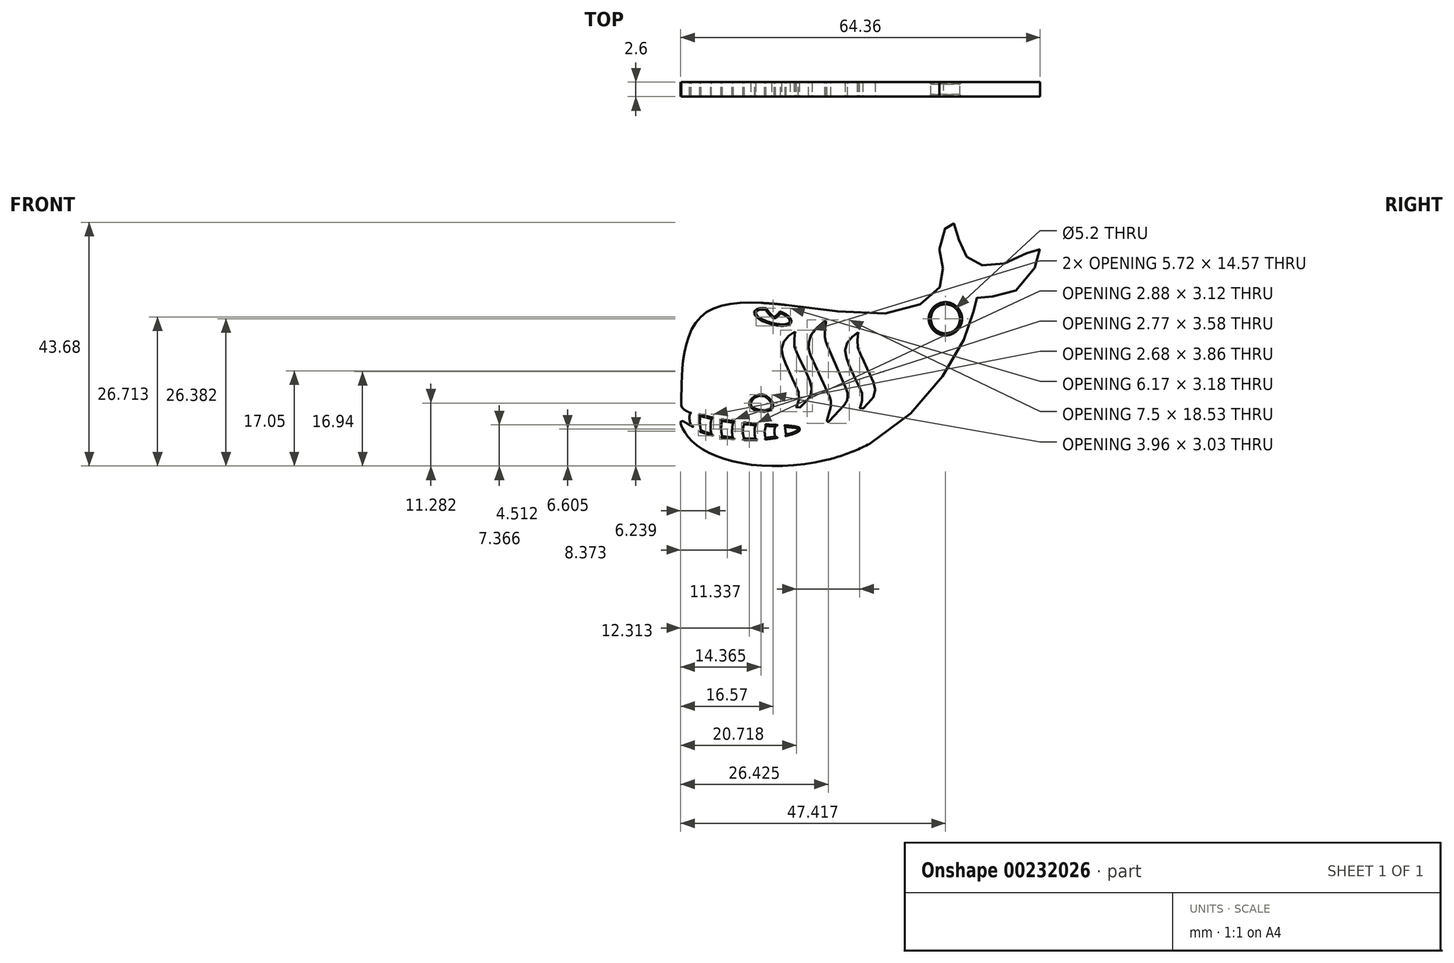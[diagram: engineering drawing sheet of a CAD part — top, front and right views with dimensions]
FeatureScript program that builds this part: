
annotation { "Feature Type Name" : "Feature", "Feature Type Description" : "" }
export const myFeature = defineFeature(function(context is Context, id is Id, definition is map)
    precondition{}
    {
        {
            var Q0;
            Q0=qCreatedBy(makeId("Front.planeOp"),FACE);
            var sketch = newSketch(context, id + "F0", { "sketchPlane" : qUnion([Q0])});
            skFitSpline(sketch, "E0", {"points": [v(-22.86, -10.44) * mm, v(-19.7, 1.07) * mm, v(5.67, 1.15) * mm, v(13.2, 5.95) * mm, v(12.7, 10.48) * mm, v(14.38, 13.69) * mm, v(15.38, 11.35) * mm, v(17.48, 8.08) * mm, v(23.08, 8.54) * mm, v(26.5, 9.96) * mm, v(23.05, 4.16) * mm, v(18, 3.34) * mm, v(17.28, 0.82) * mm, v(3.33, -16.7) * mm, v(-20.33, -17.35) * mm, v(-22.9, -13.75) * mm, v(-20.76, -14.75) * mm, v(-11.12, -16.02) * mm, v(-6.74, -14.84) * mm, v(-13.25, -14.23) * mm, v(-22.52, -12.08) * mm, v(-22.86, -10.44) * mm]});
            skFitSpline(sketch, "E1", {"points": [v(-5.34, -13.25) * mm, v(-5.6, -16.16) * mm, v(-1.36, -19.66) * mm, v(4.85, -18.8) * mm, v(4.28, -17.36) * mm, v(0.7, -15.99) * mm, v(-0.53, -13.57) * mm], "startDerivative": vector(-7.24, -19.66) * mm, "endDerivative": vector(-6.35, 20.95) * mm});
            skArc(sketch, "E2", {"start": v(-22.52, -12.08) * mm, "mid": v(-22.6, -12.94) * mm, "end": v(-22.52, -13.8) * mm});
            skArc(sketch, "E3", {"start": v(-21.63, -12.56) * mm, "mid": v(-21.72, -13.48) * mm, "end": v(-21.48, -14.38) * mm});
            skArc(sketch, "E4", {"start": v(-20.25, -13.02) * mm, "mid": v(-20.3, -14.02) * mm, "end": v(-20.15, -15) * mm});
            skArc(sketch, "E5", {"start": v(-18.7, -13.4) * mm, "mid": v(-18.83, -14.43) * mm, "end": v(-18.73, -15.45) * mm});
            skArc(sketch, "E6", {"start": v(-17.26, -13.69) * mm, "mid": v(-17.37, -14.74) * mm, "end": v(-17.22, -15.78) * mm});
            skArc(sketch, "E7", {"start": v(-15.7, -13.94) * mm, "mid": v(-15.86, -14.96) * mm, "end": v(-15.79, -15.98) * mm});
            skArc(sketch, "E8", {"start": v(-14.18, -14.13) * mm, "mid": v(-14.39, -15.11) * mm, "end": v(-14.2, -16.1) * mm});
            skArc(sketch, "E9", {"start": v(-12.64, -14.28) * mm, "mid": v(-12.77, -15.2) * mm, "end": v(-12.66, -16.11) * mm});
            skArc(sketch, "E10", {"start": v(-11.18, -14.38) * mm, "mid": v(-11.37, -15.2) * mm, "end": v(-11.23, -16.03) * mm});
            skArc(sketch, "E11", {"start": v(-9.9, -14.44) * mm, "mid": v(-10.05, -15.15) * mm, "end": v(-9.9, -15.86) * mm});
            skArc(sketch, "E12", {"start": v(-8.53, -14.52) * mm, "mid": v(-8.52, -15.04) * mm, "end": v(-8.4, -15.56) * mm});
            skFitSpline(sketch, "E13", {"points": [v(-13.24, -11.57) * mm, v(-11.8, -10.24) * mm, v(-10.5, -11.89) * mm, v(-13.24, -11.57) * mm]});
            skEllipse(sketch, "E14", {"center": v(-10.25, 0.64) * mm, "majorRadius": 2.45 * mm, "minorRadius": 0.83 * mm, "majorAxis": v(0.96, -0.26)});
            skFitSpline(sketch, "E15", {"points": [v(-10.43, 0.64) * mm, v(-14.17, 6.8) * mm, v(-14.96, 8.86) * mm, v(-10.25, 6.14) * mm, v(-3.95, 8) * mm, v(-6.2, 5.5) * mm, v(-9.66, 0.64) * mm, v(-10.43, 0.64) * mm]});
            skPoint(sketch, "E16.6.internal.snap0", {"position": v(-2.92, -13.4) * mm});
            skPoint(sketch, "E16.7.internal.snap0", {"position": v(-2.92, -13.4) * mm});
            skArc(sketch, "E17", {"start": v(-5.34, -13.25) * mm, "mid": v(-2.98, -14.05) * mm, "end": v(-0.53, -13.57) * mm});
            skLineSegment(sketch, "E18", {"start": v(-3.11, 0.02) * mm, "end": v(-4.1, -0.8) * mm});
            skLineSegment(sketch, "E19", {"start": v(-5, -4.8) * mm, "end": v(-2.45, -10.33) * mm});
            skLineSegment(sketch, "E20", {"start": v(-2.32, -11.9) * mm, "end": v(-2.79, -13.6) * mm});
            skLineSegment(sketch, "E21", {"start": v(-2.49, -13.76) * mm, "end": v(-0.46, -11.54) * mm});
            skLineSegment(sketch, "E22", {"start": v(-0.1, -9.41) * mm, "end": v(-2.8, -3.16) * mm});
            skLineSegment(sketch, "E23", {"start": v(-3.07, -1.42) * mm, "end": v(-2.92, -0.08) * mm});
            skPoint(sketch, "E24", {"position": v(-2.98, -14.05) * mm});
            skPoint(sketch, "E25.visualSharp", {"position": v(-2.98, -14.3) * mm});
            skArc(sketch, "E25.filletArc", {"start": v(-2.79, -13.6) * mm, "mid": v(-2.7, -13.8) * mm, "end": v(-2.49, -13.76) * mm});
            skPoint(sketch, "E26.visualSharp", {"position": v(0.41, -10.6) * mm});
            skArc(sketch, "E26.filletArc", {"start": v(-0.46, -11.54) * mm, "mid": v(0.04, -10.53) * mm, "end": v(-0.1, -9.41) * mm});
            skPoint(sketch, "E27.visualSharp", {"position": v(-2.1, -11.1) * mm});
            skArc(sketch, "E27.filletArc", {"start": v(-2.32, -11.9) * mm, "mid": v(-2.25, -11.1) * mm, "end": v(-2.45, -10.33) * mm});
            skArc(sketch, "E28.filletArc", {"start": v(-4.1, -0.8) * mm, "mid": v(-5.23, -2.64) * mm, "end": v(-5, -4.8) * mm});
            skPoint(sketch, "E29.visualSharp", {"position": v(-3.17, -2.33) * mm});
            skArc(sketch, "E29.filletArc", {"start": v(-3.07, -1.42) * mm, "mid": v(-3.05, -2.31) * mm, "end": v(-2.8, -3.16) * mm});
            skPoint(sketch, "E30.visualSharp", {"position": v(-2.9, 0.2) * mm});
            skArc(sketch, "E30.filletArc", {"start": v(-2.92, -0.08) * mm, "mid": v(-2.98, 0.03) * mm, "end": v(-3.11, 0.02) * mm});
            skFitSpline(sketch, "E31", {"points": [v(1.52, -1.5) * mm, v(0.32, -2.5) * mm, v(-0.29, -4.28) * mm, v(1.9, -9.56) * mm, v(2.06, -10.88) * mm, v(1.68, -12.33) * mm, v(2.58, -11.58) * mm, v(3.74, -10.17) * mm, v(3.57, -8.31) * mm, v(1.55, -3.91) * mm, v(1.42, -2.58) * mm, v(1.52, -1.5) * mm]});
            skFitSpline(sketch, "E32", {"points": [v(-7.2, -1.37) * mm, v(-8.4, -2.38) * mm, v(-9, -4.15) * mm, v(-6.82, -9.43) * mm, v(-6.66, -10.75) * mm, v(-7.04, -12.2) * mm, v(-6.14, -11.45) * mm, v(-4.98, -10.04) * mm, v(-5.15, -8.18) * mm, v(-7.17, -3.78) * mm, v(-7.3, -2.44) * mm, v(-7.2, -1.37) * mm]});
            skFitSpline(sketch, "E33.0", {"points": [v(-7.65, -0.25) * mm, v(-7.58, -0.09) * mm, v(-7.56, 0.08) * mm, v(-7.6, 0.3) * mm, v(-7.72, 0.54) * mm, v(-7.94, 0.78) * mm, v(-8.24, 1.01) * mm, v(-8.6, 1.23) * mm, v(-9.15, 1.5) * mm, v(-9.95, 1.77) * mm, v(-10.77, 1.93) * mm, v(-11.38, 1.99) * mm, v(-11.8, 1.98) * mm, v(-12.17, 1.94) * mm, v(-12.49, 1.84) * mm, v(-12.72, 1.7) * mm, v(-12.86, 1.53) * mm, v(-12.93, 1.37) * mm, v(-12.95, 1.2) * mm, v(-12.91, 0.98) * mm, v(-12.79, 0.74) * mm, v(-12.56, 0.5) * mm, v(-12.26, 0.27) * mm, v(-11.9, 0.05) * mm, v(-11.35, -0.21) * mm, v(-10.56, -0.49) * mm, v(-9.74, -0.65) * mm, v(-9.13, -0.7) * mm, v(-8.7, -0.7) * mm, v(-8.34, -0.65) * mm, v(-8.02, -0.56) * mm, v(-7.8, -0.42) * mm, v(-7.65, -0.25) * mm, v(-7.58, -0.09) * mm, v(-7.56, 0.08) * mm, v(-7.65, -0.25) * mm]});
            skCircle(sketch, "E34", {"center": v(13.53, 0.38) * mm, "radius": 2 * mm});
            skSolve(sketch);
        }
        {
            var Q0;
            Q0=makeQuery(id+"F0.imprint","IMPRINT",FACE,{"disambiguationData":[TD([[makeQuery(id+"F0.imprint","IMPRINT",EDGE,{"derivedFrom":sQuery(id+"F0.wireOp",EDGE,"E13")}),1.0]])]});
            var Q1;
            {var subQ0=sQuery(id+"F0.wireOp",EDGE,"E15");var subQ1=sQuery(id+"F0.wireOp",EDGE,"E14");var subQ2=makeQuery(id+"F0.imprint","INTERSECT",VERTEX,{"disambiguationData":[OD(0.0)],"derivedFrom":[subQ1,subQ0]});Q1=makeQuery(id+"F0.imprint","IMPRINT",FACE,{"disambiguationData":[TD([[makeQuery(id+"F0.imprint","IMPRINT",EDGE,{"disambiguationData":[TD([[subQ2,1.0]])],"derivedFrom":subQ1}),1.0]])]});}
            var Q2;
            {var subQ0=sQuery(id+"F0.wireOp",EDGE,"E3");Q2=makeQuery(id+"F0.imprint","IMPRINT",FACE,{"disambiguationData":[TD([[makeQuery(id+"F0.imprint","IMPRINT",EDGE,{"derivedFrom":subQ0}),1.0]])]});}
            var Q3;
            {var subQ0=sQuery(id+"F0.wireOp",EDGE,"E5");Q3=makeQuery(id+"F0.imprint","IMPRINT",FACE,{"disambiguationData":[TD([[makeQuery(id+"F0.imprint","IMPRINT",EDGE,{"derivedFrom":subQ0}),1.0]])]});}
            var Q4;
            {var subQ0=sQuery(id+"F0.wireOp",EDGE,"E7");Q4=makeQuery(id+"F0.imprint","IMPRINT",FACE,{"disambiguationData":[TD([[makeQuery(id+"F0.imprint","IMPRINT",EDGE,{"derivedFrom":subQ0}),1.0]])]});}
            var Q5;
            {var subQ0=sQuery(id+"F0.wireOp",EDGE,"E9");Q5=makeQuery(id+"F0.imprint","IMPRINT",FACE,{"disambiguationData":[TD([[makeQuery(id+"F0.imprint","IMPRINT",EDGE,{"derivedFrom":subQ0}),1.0]])]});}
            var Q6;
            {var subQ0=sQuery(id+"F0.wireOp",EDGE,"E11");Q6=makeQuery(id+"F0.imprint","IMPRINT",FACE,{"disambiguationData":[TD([[makeQuery(id+"F0.imprint","IMPRINT",EDGE,{"derivedFrom":subQ0}),1.0]])]});}
            var Q7;
            {var subQ0=sQuery(id+"F0.wireOp",EDGE,"E17");Q7=makeQuery(id+"F0.imprint","IMPRINT",FACE,{"disambiguationData":[TD([[makeQuery(id+"F0.imprint","IMPRINT",EDGE,{"derivedFrom":subQ0}),-1.0]])]});}
            var Q8;
            {var subQ0=sQuery(id+"F0.wireOp",EDGE,"E15");var subQ1=sQuery(id+"F0.wireOp",EDGE,"E0");var subQ2=makeQuery(id+"F0.imprint","INTERSECT",VERTEX,{"disambiguationData":[OD(0.0)],"derivedFrom":[subQ1,subQ0]});Q8=makeQuery(id+"F0.imprint","IMPRINT",FACE,{"disambiguationData":[TD([[makeQuery(id+"F0.imprint","IMPRINT",EDGE,{"disambiguationData":[TD([[subQ2,-1.0]])],"derivedFrom":subQ1}),1.0]])]});}
            var Q9;
            {var subQ0=sQuery(id+"F0.wireOp",EDGE,"E15");var subQ1=sQuery(id+"F0.wireOp",EDGE,"E0");var subQ2=makeQuery(id+"F0.imprint","INTERSECT",VERTEX,{"disambiguationData":[OD(0.0)],"derivedFrom":[subQ1,subQ0]});Q9=makeQuery(id+"F0.imprint","IMPRINT",FACE,{"disambiguationData":[TD([[makeQuery(id+"F0.imprint","IMPRINT",EDGE,{"disambiguationData":[TD([[subQ2,-1.0]])],"derivedFrom":subQ1}),-1.0]])]});}
            var Q10;
            {var subQ0=sQuery(id+"F0.wireOp",EDGE,"E15");var subQ1=sQuery(id+"F0.wireOp",EDGE,"E14");var subQ2=makeQuery(id+"F0.imprint","INTERSECT",VERTEX,{"disambiguationData":[OD(0.0)],"derivedFrom":[subQ1,subQ0]});Q10=makeQuery(id+"F0.imprint","IMPRINT",FACE,{"disambiguationData":[TD([[makeQuery(id+"F0.imprint","IMPRINT",EDGE,{"disambiguationData":[TD([[subQ2,-1.0]])],"derivedFrom":subQ1}),-1.0]])]});}
            var Q11;
            {var subQ0=sQuery(id+"F0.wireOp",EDGE,"E15");var subQ1=sQuery(id+"F0.wireOp",EDGE,"E14");var subQ2=makeQuery(id+"F0.imprint","INTERSECT",VERTEX,{"disambiguationData":[OD(0.0)],"derivedFrom":[subQ1,subQ0]});Q11=makeQuery(id+"F0.imprint","IMPRINT",FACE,{"disambiguationData":[TD([[makeQuery(id+"F0.imprint","IMPRINT",EDGE,{"disambiguationData":[TD([[subQ2,1.0]])],"derivedFrom":subQ1}),-1.0]])]});}
            extrude(context, id + "F1", {"entities" : qUnion([Q0, Q1, Q2, Q3, Q4, Q5, Q6, Q7, Q8, Q9, Q10, Q11]), "endBound" : BoundingType.SYMMETRIC, "depth" : 2 * mm});
        }
        {
            var Q0;
            Q0=makeQuery(id+"F1.opExtrude","CAP_EDGE",EDGE,{"disambiguationData":[OSD([sQuery(id+"F0.wireOp",EDGE,"E13")])],"isStart":false});
            var Q1;
            Q1=makeQuery(id+"F1.opExtrude","CAP_EDGE",EDGE,{"disambiguationData":[OSD([sQuery(id+"F0.wireOp",EDGE,"E13")])],"isStart":true});
            fillet(context, id + "F2", {"entities" : qUnion([Q0, Q1]), "radius" : .2 * mm, "tangentPropagation" : true, "allowEdgeOverflow" : false});
        }
        {
            var Q0;
            Q0=makeQuery(id+"F1.opExtrude","CAP_EDGE",EDGE,{"disambiguationData":[OSD([sQuery(id+"F0.wireOp",EDGE,"E34")])],"isStart":false});
            var Q1;
            Q1=makeQuery(id+"F1.opExtrude","CAP_EDGE",EDGE,{"disambiguationData":[OSD([sQuery(id+"F0.wireOp",EDGE,"E34")])],"isStart":true});
            chamfer(context, id + "F3", {"entities" : qUnion([Q0, Q1]), "width" : .3 * mm, "tangentPropagation" : true});
        }
        {
            var Q0;
            Q0=makeQuery(id+"F1.opExtrude","CAP_EDGE",EDGE,{"disambiguationData":[OSD([sQuery(id+"F0.wireOp",EDGE,"E32")])],"isStart":false});
            var Q1;
            Q1=makeQuery(id+"F1.opExtrude","CAP_EDGE",EDGE,{"disambiguationData":[OSD([sQuery(id+"F0.wireOp",EDGE,"E19")])],"isStart":false});
            var Q2;
            Q2=makeQuery(id+"F1.opExtrude","CAP_EDGE",EDGE,{"disambiguationData":[OSD([sQuery(id+"F0.wireOp",EDGE,"E31")])],"isStart":false});
            var Q3;
            Q3=makeQuery(id+"F1.opExtrude","CAP_EDGE",EDGE,{"disambiguationData":[OSD([sQuery(id+"F0.wireOp",EDGE,"E31")])],"isStart":true});
            var Q4;
            Q4=makeQuery(id+"F1.opExtrude","CAP_EDGE",EDGE,{"disambiguationData":[OSD([sQuery(id+"F0.wireOp",EDGE,"E22")])],"isStart":true});
            var Q5;
            Q5=makeQuery(id+"F1.opExtrude","CAP_EDGE",EDGE,{"disambiguationData":[OSD([sQuery(id+"F0.wireOp",EDGE,"E32")])],"isStart":true});
            var Q6;
            Q6=makeQuery(id+"F1.opExtrude","CAP_EDGE",EDGE,{"disambiguationData":[OSD([sQuery(id+"F0.wireOp",EDGE,"E14")])],"isStart":false});
            var Q7;
            {var subQ0=sQuery(id+"F0.wireOp",EDGE,"E15");var subQ1=sQuery(id+"F0.wireOp",EDGE,"E14");Q7=makeQuery(id+"F1.opExtrude","CAP_EDGE",EDGE,{"disambiguationData":[OSD([subQ0]),TDD([makeQuery(id+"F0.imprint","IMPRINT",EDGE,{"disambiguationData":[TD([[makeQuery(id+"F0.imprint","INTERSECT",VERTEX,{"disambiguationData":[OD(0.0)],"derivedFrom":[subQ1,subQ0]}),1.0]])],"derivedFrom":subQ0})])],"isStart":false});}
            var Q8;
            Q8=makeQuery(id+"F1.opExtrude","CAP_EDGE",EDGE,{"disambiguationData":[OSD([sQuery(id+"F0.wireOp",EDGE,"E14")])],"isStart":true});
            var Q9;
            {var subQ0=sQuery(id+"F0.wireOp",EDGE,"E15");var subQ1=sQuery(id+"F0.wireOp",EDGE,"E14");Q9=makeQuery(id+"F1.opExtrude","CAP_EDGE",EDGE,{"disambiguationData":[OSD([subQ0]),TDD([makeQuery(id+"F0.imprint","IMPRINT",EDGE,{"disambiguationData":[TD([[makeQuery(id+"F0.imprint","INTERSECT",VERTEX,{"disambiguationData":[OD(0.0)],"derivedFrom":[subQ1,subQ0]}),1.0]])],"derivedFrom":subQ0})])],"isStart":true});}
            var Q10;
            {var subQ0=sQuery(id+"F0.wireOp",EDGE,"E0");Q10=makeQuery(id+"F1.opExtrude","CAP_EDGE",EDGE,{"disambiguationData":[OSD([subQ0]),TDD([makeQuery(id+"F0.imprint","IMPRINT",EDGE,{"disambiguationData":[TD([[makeQuery(id+"F0.imprint","INTERSECT",VERTEX,{"disambiguationData":[OD(1.0)],"derivedFrom":[subQ0,sQuery(id+"F0.wireOp",EDGE,"E10")]}),-1.0]])],"derivedFrom":subQ0})])],"isStart":true});}
            var Q11;
            Q11=makeQuery(id+"F1.opExtrude","CAP_EDGE",EDGE,{"disambiguationData":[OSD([sQuery(id+"F0.wireOp",EDGE,"E10")])],"isStart":true});
            var Q12;
            {var subQ0=sQuery(id+"F0.wireOp",EDGE,"E0");Q12=makeQuery(id+"F1.opExtrude","CAP_EDGE",EDGE,{"disambiguationData":[OSD([subQ0]),TDD([makeQuery(id+"F0.imprint","IMPRINT",EDGE,{"disambiguationData":[TD([[makeQuery(id+"F0.imprint","INTERSECT",VERTEX,{"disambiguationData":[OD(0.0)],"derivedFrom":[subQ0,sQuery(id+"F0.wireOp",EDGE,"E10")]}),1.0]])],"derivedFrom":subQ0})])],"isStart":true});}
            var Q13;
            Q13=makeQuery(id+"F1.opExtrude","CAP_EDGE",EDGE,{"disambiguationData":[OSD([sQuery(id+"F0.wireOp",EDGE,"E11")])],"isStart":true});
            var Q14;
            Q14=makeQuery(id+"F1.opExtrude","CAP_EDGE",EDGE,{"disambiguationData":[OSD([sQuery(id+"F0.wireOp",EDGE,"E12")])],"isStart":true});
            var Q15;
            {var subQ0=sQuery(id+"F0.wireOp",EDGE,"E12");var subQ1=sQuery(id+"F0.wireOp",EDGE,"E0");Q15=makeQuery(id+"F1.opExtrude","CAP_EDGE",EDGE,{"disambiguationData":[OSD([subQ1]),TDD([makeQuery(id+"F0.imprint","IMPRINT",EDGE,{"disambiguationData":[TD([[makeQuery(id+"F0.imprint","INTERSECT",VERTEX,{"disambiguationData":[OD(0.0)],"derivedFrom":[subQ1,subQ0]}),1.0]])],"derivedFrom":subQ1})])],"isStart":true});}
            var Q16;
            {var subQ0=sQuery(id+"F0.wireOp",EDGE,"E0");Q16=makeQuery(id+"F1.opExtrude","CAP_EDGE",EDGE,{"disambiguationData":[OSD([subQ0]),TDD([makeQuery(id+"F0.imprint","IMPRINT",EDGE,{"disambiguationData":[TD([[makeQuery(id+"F0.imprint","INTERSECT",VERTEX,{"disambiguationData":[OD(0.0)],"derivedFrom":[subQ0,sQuery(id+"F0.wireOp",EDGE,"E8")]}),1.0]])],"derivedFrom":subQ0})])],"isStart":true});}
            var Q17;
            Q17=makeQuery(id+"F1.opExtrude","CAP_EDGE",EDGE,{"disambiguationData":[OSD([sQuery(id+"F0.wireOp",EDGE,"E8")])],"isStart":true});
            var Q18;
            {var subQ0=sQuery(id+"F0.wireOp",EDGE,"E0");Q18=makeQuery(id+"F1.opExtrude","CAP_EDGE",EDGE,{"disambiguationData":[OSD([subQ0]),TDD([makeQuery(id+"F0.imprint","IMPRINT",EDGE,{"disambiguationData":[TD([[makeQuery(id+"F0.imprint","INTERSECT",VERTEX,{"disambiguationData":[OD(1.0)],"derivedFrom":[subQ0,sQuery(id+"F0.wireOp",EDGE,"E8")]}),-1.0]])],"derivedFrom":subQ0})])],"isStart":true});}
            var Q19;
            Q19=makeQuery(id+"F1.opExtrude","CAP_EDGE",EDGE,{"disambiguationData":[OSD([sQuery(id+"F0.wireOp",EDGE,"E9")])],"isStart":true});
            var Q20;
            Q20=makeQuery(id+"F1.opExtrude","CAP_EDGE",EDGE,{"disambiguationData":[OSD([sQuery(id+"F0.wireOp",EDGE,"E7")])],"isStart":true});
            var Q21;
            {var subQ0=sQuery(id+"F0.wireOp",EDGE,"E0");Q21=makeQuery(id+"F1.opExtrude","CAP_EDGE",EDGE,{"disambiguationData":[OSD([subQ0]),TDD([makeQuery(id+"F0.imprint","IMPRINT",EDGE,{"disambiguationData":[TD([[makeQuery(id+"F0.imprint","INTERSECT",VERTEX,{"disambiguationData":[OD(0.0)],"derivedFrom":[subQ0,sQuery(id+"F0.wireOp",EDGE,"E6")]}),1.0]])],"derivedFrom":subQ0})])],"isStart":true});}
            var Q22;
            Q22=makeQuery(id+"F1.opExtrude","CAP_EDGE",EDGE,{"disambiguationData":[OSD([sQuery(id+"F0.wireOp",EDGE,"E6")])],"isStart":true});
            var Q23;
            {var subQ0=sQuery(id+"F0.wireOp",EDGE,"E0");Q23=makeQuery(id+"F1.opExtrude","CAP_EDGE",EDGE,{"disambiguationData":[OSD([subQ0]),TDD([makeQuery(id+"F0.imprint","IMPRINT",EDGE,{"disambiguationData":[TD([[makeQuery(id+"F0.imprint","INTERSECT",VERTEX,{"disambiguationData":[OD(1.0)],"derivedFrom":[subQ0,sQuery(id+"F0.wireOp",EDGE,"E6")]}),-1.0]])],"derivedFrom":subQ0})])],"isStart":true});}
            var Q24;
            {var subQ0=sQuery(id+"F0.wireOp",EDGE,"E0");Q24=makeQuery(id+"F1.opExtrude","CAP_EDGE",EDGE,{"disambiguationData":[OSD([subQ0]),TDD([makeQuery(id+"F0.imprint","IMPRINT",EDGE,{"disambiguationData":[TD([[makeQuery(id+"F0.imprint","INTERSECT",VERTEX,{"disambiguationData":[OD(1.0)],"derivedFrom":[subQ0,sQuery(id+"F0.wireOp",EDGE,"E4")]}),-1.0]])],"derivedFrom":subQ0})])],"isStart":true});}
            var Q25;
            Q25=makeQuery(id+"F1.opExtrude","CAP_EDGE",EDGE,{"disambiguationData":[OSD([sQuery(id+"F0.wireOp",EDGE,"E4")])],"isStart":true});
            var Q26;
            {var subQ0=sQuery(id+"F0.wireOp",EDGE,"E0");Q26=makeQuery(id+"F1.opExtrude","CAP_EDGE",EDGE,{"disambiguationData":[OSD([subQ0]),TDD([makeQuery(id+"F0.imprint","IMPRINT",EDGE,{"disambiguationData":[TD([[makeQuery(id+"F0.imprint","INTERSECT",VERTEX,{"disambiguationData":[OD(0.0)],"derivedFrom":[subQ0,sQuery(id+"F0.wireOp",EDGE,"E4")]}),1.0]])],"derivedFrom":subQ0})])],"isStart":true});}
            var Q27;
            Q27=makeQuery(id+"F1.opExtrude","CAP_EDGE",EDGE,{"disambiguationData":[OSD([sQuery(id+"F0.wireOp",EDGE,"E5")])],"isStart":true});
            var Q28;
            Q28=makeQuery(id+"F1.opExtrude","CAP_EDGE",EDGE,{"disambiguationData":[OSD([sQuery(id+"F0.wireOp",EDGE,"E3")])],"isStart":true});
            var Q29;
            Q29=makeQuery(id+"F1.opExtrude","CAP_EDGE",EDGE,{"disambiguationData":[OSD([sQuery(id+"F0.wireOp",EDGE,"E3")])],"isStart":false});
            var Q30;
            {var subQ0=sQuery(id+"F0.wireOp",EDGE,"E0");Q30=makeQuery(id+"F1.opExtrude","CAP_EDGE",EDGE,{"disambiguationData":[OSD([subQ0]),TDD([makeQuery(id+"F0.imprint","IMPRINT",EDGE,{"disambiguationData":[TD([[makeQuery(id+"F0.imprint","INTERSECT",VERTEX,{"disambiguationData":[OD(0.0)],"derivedFrom":[subQ0,sQuery(id+"F0.wireOp",EDGE,"E4")]}),1.0]])],"derivedFrom":subQ0})])],"isStart":false});}
            var Q31;
            Q31=makeQuery(id+"F1.opExtrude","CAP_EDGE",EDGE,{"disambiguationData":[OSD([sQuery(id+"F0.wireOp",EDGE,"E5")])],"isStart":false});
            var Q32;
            Q32=makeQuery(id+"F1.opExtrude","CAP_EDGE",EDGE,{"disambiguationData":[OSD([sQuery(id+"F0.wireOp",EDGE,"E4")])],"isStart":false});
            var Q33;
            {var subQ0=sQuery(id+"F0.wireOp",EDGE,"E0");Q33=makeQuery(id+"F1.opExtrude","CAP_EDGE",EDGE,{"disambiguationData":[OSD([subQ0]),TDD([makeQuery(id+"F0.imprint","IMPRINT",EDGE,{"disambiguationData":[TD([[makeQuery(id+"F0.imprint","INTERSECT",VERTEX,{"disambiguationData":[OD(1.0)],"derivedFrom":[subQ0,sQuery(id+"F0.wireOp",EDGE,"E4")]}),-1.0]])],"derivedFrom":subQ0})])],"isStart":false});}
            var Q34;
            {var subQ0=sQuery(id+"F0.wireOp",EDGE,"E0");Q34=makeQuery(id+"F1.opExtrude","CAP_EDGE",EDGE,{"disambiguationData":[OSD([subQ0]),TDD([makeQuery(id+"F0.imprint","IMPRINT",EDGE,{"disambiguationData":[TD([[makeQuery(id+"F0.imprint","INTERSECT",VERTEX,{"disambiguationData":[OD(0.0)],"derivedFrom":[subQ0,sQuery(id+"F0.wireOp",EDGE,"E6")]}),1.0]])],"derivedFrom":subQ0})])],"isStart":false});}
            var Q35;
            Q35=makeQuery(id+"F1.opExtrude","CAP_EDGE",EDGE,{"disambiguationData":[OSD([sQuery(id+"F0.wireOp",EDGE,"E6")])],"isStart":false});
            var Q36;
            {var subQ0=sQuery(id+"F0.wireOp",EDGE,"E0");Q36=makeQuery(id+"F1.opExtrude","CAP_EDGE",EDGE,{"disambiguationData":[OSD([subQ0]),TDD([makeQuery(id+"F0.imprint","IMPRINT",EDGE,{"disambiguationData":[TD([[makeQuery(id+"F0.imprint","INTERSECT",VERTEX,{"disambiguationData":[OD(1.0)],"derivedFrom":[subQ0,sQuery(id+"F0.wireOp",EDGE,"E6")]}),-1.0]])],"derivedFrom":subQ0})])],"isStart":false});}
            var Q37;
            Q37=makeQuery(id+"F1.opExtrude","CAP_EDGE",EDGE,{"disambiguationData":[OSD([sQuery(id+"F0.wireOp",EDGE,"E7")])],"isStart":false});
            var Q38;
            {var subQ0=sQuery(id+"F0.wireOp",EDGE,"E0");Q38=makeQuery(id+"F1.opExtrude","CAP_EDGE",EDGE,{"disambiguationData":[OSD([subQ0]),TDD([makeQuery(id+"F0.imprint","IMPRINT",EDGE,{"disambiguationData":[TD([[makeQuery(id+"F0.imprint","INTERSECT",VERTEX,{"disambiguationData":[OD(0.0)],"derivedFrom":[subQ0,sQuery(id+"F0.wireOp",EDGE,"E8")]}),1.0]])],"derivedFrom":subQ0})])],"isStart":false});}
            var Q39;
            Q39=makeQuery(id+"F1.opExtrude","CAP_EDGE",EDGE,{"disambiguationData":[OSD([sQuery(id+"F0.wireOp",EDGE,"E9")])],"isStart":false});
            var Q40;
            Q40=makeQuery(id+"F1.opExtrude","CAP_EDGE",EDGE,{"disambiguationData":[OSD([sQuery(id+"F0.wireOp",EDGE,"E8")])],"isStart":false});
            var Q41;
            {var subQ0=sQuery(id+"F0.wireOp",EDGE,"E0");Q41=makeQuery(id+"F1.opExtrude","CAP_EDGE",EDGE,{"disambiguationData":[OSD([subQ0]),TDD([makeQuery(id+"F0.imprint","IMPRINT",EDGE,{"disambiguationData":[TD([[makeQuery(id+"F0.imprint","INTERSECT",VERTEX,{"disambiguationData":[OD(1.0)],"derivedFrom":[subQ0,sQuery(id+"F0.wireOp",EDGE,"E8")]}),-1.0]])],"derivedFrom":subQ0})])],"isStart":false});}
            var Q42;
            {var subQ0=sQuery(id+"F0.wireOp",EDGE,"E0");Q42=makeQuery(id+"F1.opExtrude","CAP_EDGE",EDGE,{"disambiguationData":[OSD([subQ0]),TDD([makeQuery(id+"F0.imprint","IMPRINT",EDGE,{"disambiguationData":[TD([[makeQuery(id+"F0.imprint","INTERSECT",VERTEX,{"disambiguationData":[OD(0.0)],"derivedFrom":[subQ0,sQuery(id+"F0.wireOp",EDGE,"E10")]}),1.0]])],"derivedFrom":subQ0})])],"isStart":false});}
            var Q43;
            Q43=makeQuery(id+"F1.opExtrude","CAP_EDGE",EDGE,{"disambiguationData":[OSD([sQuery(id+"F0.wireOp",EDGE,"E11")])],"isStart":false});
            var Q44;
            Q44=makeQuery(id+"F1.opExtrude","CAP_EDGE",EDGE,{"disambiguationData":[OSD([sQuery(id+"F0.wireOp",EDGE,"E10")])],"isStart":false});
            var Q45;
            {var subQ0=sQuery(id+"F0.wireOp",EDGE,"E0");Q45=makeQuery(id+"F1.opExtrude","CAP_EDGE",EDGE,{"disambiguationData":[OSD([subQ0]),TDD([makeQuery(id+"F0.imprint","IMPRINT",EDGE,{"disambiguationData":[TD([[makeQuery(id+"F0.imprint","INTERSECT",VERTEX,{"disambiguationData":[OD(1.0)],"derivedFrom":[subQ0,sQuery(id+"F0.wireOp",EDGE,"E10")]}),-1.0]])],"derivedFrom":subQ0})])],"isStart":false});}
            var Q46;
            {var subQ0=sQuery(id+"F0.wireOp",EDGE,"E12");var subQ1=sQuery(id+"F0.wireOp",EDGE,"E0");Q46=makeQuery(id+"F1.opExtrude","CAP_EDGE",EDGE,{"disambiguationData":[OSD([subQ1]),TDD([makeQuery(id+"F0.imprint","IMPRINT",EDGE,{"disambiguationData":[TD([[makeQuery(id+"F0.imprint","INTERSECT",VERTEX,{"disambiguationData":[OD(0.0)],"derivedFrom":[subQ1,subQ0]}),1.0]])],"derivedFrom":subQ1})])],"isStart":false});}
            var Q47;
            Q47=makeQuery(id+"F1.opExtrude","CAP_EDGE",EDGE,{"disambiguationData":[OSD([sQuery(id+"F0.wireOp",EDGE,"E12")])],"isStart":false});
            fillet(context, id + "F4", {"entities" : qUnion([Q0, Q1, Q2, Q3, Q4, Q5, Q6, Q7, Q8, Q9, Q10, Q11, Q12, Q13, Q14, Q15, Q16, Q17, Q18, Q19, Q20, Q21, Q22, Q23, Q24, Q25, Q26, Q27, Q28, Q29, Q30, Q31, Q32, Q33, Q34, Q35, Q36, Q37, Q38, Q39, Q40, Q41, Q42, Q43, Q44, Q45, Q46, Q47]), "radius" : .2 * mm, "tangentPropagation" : true, "allowEdgeOverflow" : false});
        }
        {
            var Q0;
            Q0=makeQuery(id+"F1.opExtrude","SWEPT_BODY",BODY,{"disambiguationData":[OSD([sQuery(id+"F0.wireOp",EDGE,"E0"),sQuery(id+"F0.wireOp",EDGE,"E1"),sQuery(id+"F0.wireOp",EDGE,"E3"),sQuery(id+"F0.wireOp",EDGE,"E4"),sQuery(id+"F0.wireOp",EDGE,"E5"),sQuery(id+"F0.wireOp",EDGE,"E6"),sQuery(id+"F0.wireOp",EDGE,"E7"),sQuery(id+"F0.wireOp",EDGE,"E8"),sQuery(id+"F0.wireOp",EDGE,"E9"),sQuery(id+"F0.wireOp",EDGE,"E10"),sQuery(id+"F0.wireOp",EDGE,"E11"),sQuery(id+"F0.wireOp",EDGE,"E12"),sQuery(id+"F0.wireOp",EDGE,"E13"),sQuery(id+"F0.wireOp",EDGE,"E14"),sQuery(id+"F0.wireOp",EDGE,"E15"),sQuery(id+"F0.wireOp",EDGE,"E18"),sQuery(id+"F0.wireOp",EDGE,"E19"),sQuery(id+"F0.wireOp",EDGE,"E20"),sQuery(id+"F0.wireOp",EDGE,"E21"),sQuery(id+"F0.wireOp",EDGE,"E22"),sQuery(id+"F0.wireOp",EDGE,"E23"),sQuery(id+"F0.wireOp",EDGE,"E25.filletArc"),sQuery(id+"F0.wireOp",EDGE,"E26.filletArc"),sQuery(id+"F0.wireOp",EDGE,"E27.filletArc"),sQuery(id+"F0.wireOp",EDGE,"E28.filletArc"),sQuery(id+"F0.wireOp",EDGE,"E29.filletArc"),sQuery(id+"F0.wireOp",EDGE,"E30.filletArc"),sQuery(id+"F0.wireOp",EDGE,"E31"),sQuery(id+"F0.wireOp",EDGE,"E32"),sQuery(id+"F0.wireOp",EDGE,"E34")])]});
            var Q1;
            {var subQ0=sQuery(id+"F0.wireOp",EDGE,"E3");var subQ1=sQuery(id+"F0.wireOp",EDGE,"E1");var subQ2=sQuery(id+"F0.wireOp",EDGE,"E0");var subQ3=makeQuery(id+"F0.imprint","INTERSECT",VERTEX,{"disambiguationData":[OD(1.0)],"derivedFrom":[subQ2,sQuery(id+"F0.wireOp",EDGE,"E2")]});Q1=makeQuery(id+"F4.opFillet","BLEND_VERTEX",VERTEX,{"blendedFrom":[makeQuery(id+"F1.opExtrude","CAP_EDGE",EDGE,{"disambiguationData":[OSD([subQ0])],"isStart":false}),makeQuery(id+"F1.opExtrude","SWEPT_FACE",FACE,{"disambiguationData":[OSD([subQ2]),TDD([makeQuery(id+"F0.imprint","IMPRINT",EDGE,{"disambiguationData":[TD([[subQ3,1.0]])],"derivedFrom":subQ2}),makeQuery(id+"F0.imprint","IMPRINT",EDGE,{"disambiguationData":[TD([[subQ3,-1.0]])],"derivedFrom":subQ2})])]}),makeQuery(id+"F1.opExtrude","CAP_FACE",FACE,{"disambiguationData":[OSD([subQ2,subQ1,subQ0,sQuery(id+"F0.wireOp",EDGE,"E4"),sQuery(id+"F0.wireOp",EDGE,"E5"),sQuery(id+"F0.wireOp",EDGE,"E6"),sQuery(id+"F0.wireOp",EDGE,"E7"),sQuery(id+"F0.wireOp",EDGE,"E8"),sQuery(id+"F0.wireOp",EDGE,"E9"),sQuery(id+"F0.wireOp",EDGE,"E10"),sQuery(id+"F0.wireOp",EDGE,"E11"),sQuery(id+"F0.wireOp",EDGE,"E12"),sQuery(id+"F0.wireOp",EDGE,"E13"),sQuery(id+"F0.wireOp",EDGE,"E14"),sQuery(id+"F0.wireOp",EDGE,"E15"),sQuery(id+"F0.wireOp",EDGE,"E18"),sQuery(id+"F0.wireOp",EDGE,"E19"),sQuery(id+"F0.wireOp",EDGE,"E20"),sQuery(id+"F0.wireOp",EDGE,"E21"),sQuery(id+"F0.wireOp",EDGE,"E22"),sQuery(id+"F0.wireOp",EDGE,"E23"),sQuery(id+"F0.wireOp",EDGE,"E25.filletArc"),sQuery(id+"F0.wireOp",EDGE,"E26.filletArc"),sQuery(id+"F0.wireOp",EDGE,"E27.filletArc"),sQuery(id+"F0.wireOp",EDGE,"E28.filletArc"),sQuery(id+"F0.wireOp",EDGE,"E29.filletArc"),sQuery(id+"F0.wireOp",EDGE,"E30.filletArc"),sQuery(id+"F0.wireOp",EDGE,"E31"),sQuery(id+"F0.wireOp",EDGE,"E32"),sQuery(id+"F0.wireOp",EDGE,"E34")])],"isStart":false})],"blendedInto":[makeQuery(id+"F1.opExtrude","SWEPT_FACE",FACE,{"disambiguationData":[OSD([subQ2]),TDD([makeQuery(id+"F0.imprint","IMPRINT",EDGE,{"disambiguationData":[TD([[subQ3,1.0]])],"derivedFrom":subQ2}),makeQuery(id+"F0.imprint","IMPRINT",EDGE,{"disambiguationData":[TD([[subQ3,-1.0]])],"derivedFrom":subQ2})])]}),makeQuery(id+"F1.opExtrude","CAP_FACE",FACE,{"disambiguationData":[OSD([subQ2,subQ1,subQ0,sQuery(id+"F0.wireOp",EDGE,"E4"),sQuery(id+"F0.wireOp",EDGE,"E5"),sQuery(id+"F0.wireOp",EDGE,"E6"),sQuery(id+"F0.wireOp",EDGE,"E7"),sQuery(id+"F0.wireOp",EDGE,"E8"),sQuery(id+"F0.wireOp",EDGE,"E9"),sQuery(id+"F0.wireOp",EDGE,"E10"),sQuery(id+"F0.wireOp",EDGE,"E11"),sQuery(id+"F0.wireOp",EDGE,"E12"),sQuery(id+"F0.wireOp",EDGE,"E13"),sQuery(id+"F0.wireOp",EDGE,"E14"),sQuery(id+"F0.wireOp",EDGE,"E15"),sQuery(id+"F0.wireOp",EDGE,"E18"),sQuery(id+"F0.wireOp",EDGE,"E19"),sQuery(id+"F0.wireOp",EDGE,"E20"),sQuery(id+"F0.wireOp",EDGE,"E21"),sQuery(id+"F0.wireOp",EDGE,"E22"),sQuery(id+"F0.wireOp",EDGE,"E23"),sQuery(id+"F0.wireOp",EDGE,"E25.filletArc"),sQuery(id+"F0.wireOp",EDGE,"E26.filletArc"),sQuery(id+"F0.wireOp",EDGE,"E27.filletArc"),sQuery(id+"F0.wireOp",EDGE,"E28.filletArc"),sQuery(id+"F0.wireOp",EDGE,"E29.filletArc"),sQuery(id+"F0.wireOp",EDGE,"E30.filletArc"),sQuery(id+"F0.wireOp",EDGE,"E31"),sQuery(id+"F0.wireOp",EDGE,"E32"),sQuery(id+"F0.wireOp",EDGE,"E34")])],"isStart":false})]});}
            transform(context, id + "F5", {"entities" : qUnion([Q0]), "transformType" : TransformType.SCALE_UNIFORMLY, "scale" : 1.3, "scalePoint" : qUnion([Q1]), "makeCopy" : false});
        }
    });
